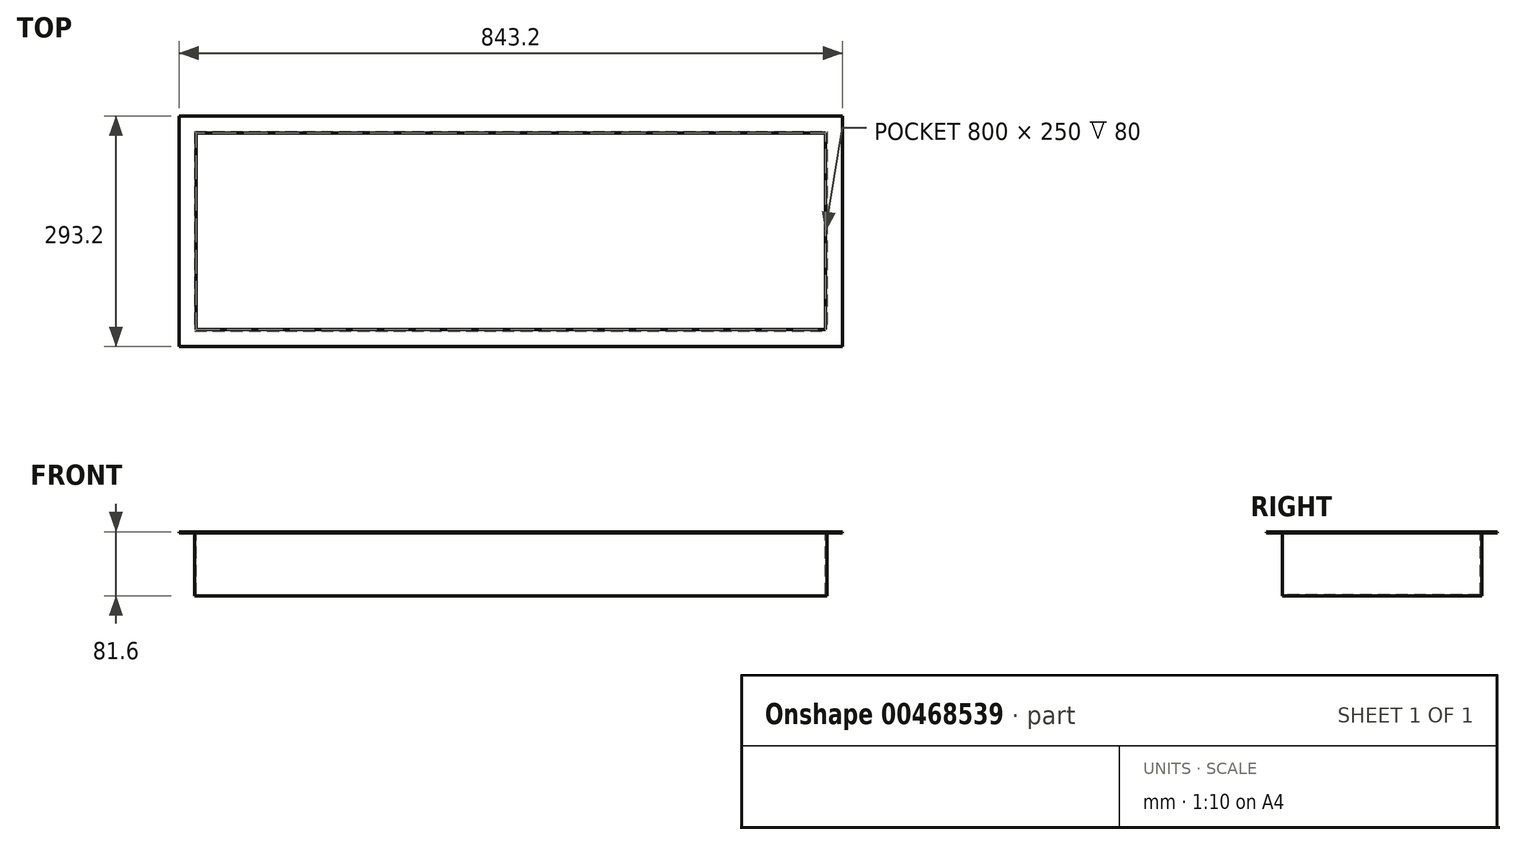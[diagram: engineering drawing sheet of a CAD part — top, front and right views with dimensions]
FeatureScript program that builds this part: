
annotation { "Feature Type Name" : "Feature", "Feature Type Description" : "" }
export const myFeature = defineFeature(function(context is Context, id is Id, definition is map)
    precondition{}
    {
        {
            var Q0;
            Q0=qCreatedBy(makeId("Top.planeOp"),FACE);
            var sketch = newSketch(context, id + "F0", { "sketchPlane" : qUnion([Q0])});
            skLineSegment(sketch, "E0.bottom", {"start": v(-398.97, -30.52) * mm, "end": v(404.23, -30.52) * mm});
            skLineSegment(sketch, "E0.top", {"start": v(-398.97, -283.72) * mm, "end": v(404.23, -283.72) * mm});
            skLineSegment(sketch, "E0.left", {"start": v(-398.97, -30.52) * mm, "end": v(-398.97, -283.72) * mm});
            skLineSegment(sketch, "E0.right", {"start": v(404.23, -30.52) * mm, "end": v(404.23, -283.72) * mm});
            skSolve(sketch);
        }
        {
            var Q0;
            Q0 = qSketchRegion(id + "F0", true);
            extrude(context, id + "F1", {"entities" : qUnion([Q0]), "depth" : 80 * mm, "offsetDistance" : 25 * mm});
        }
        {
            var Q0;
            Q0=makeQuery(id+"F1.opExtrude","CAP_FACE",FACE,{"disambiguationData":[OSD([sQuery(id+"F0.wireOp",EDGE,"E0.bottom"),sQuery(id+"F0.wireOp",EDGE,"E0.top"),sQuery(id+"F0.wireOp",EDGE,"E0.left"),sQuery(id+"F0.wireOp",EDGE,"E0.right")])],"isStart":false});
            var sketch = newSketch(context, id + "F2", { "sketchPlane" : qUnion([Q0])});
            skPoint(sketch, "E1", {"position": v(-398.97, -157.12) * mm});
            skPoint(sketch, "E2", {"position": v(404.23, -157.12) * mm});
            skPoint(sketch, "E3", {"position": v(0, -283.72) * mm});
            skPoint(sketch, "E4", {"position": v(2.63, -30.52) * mm});
            skLineSegment(sketch, "E5", {"start": v(2.63, -30.52) * mm, "end": v(0, -283.72) * mm, "construction": true});
            skLineSegment(sketch, "E6", {"start": v(-398.97, -157.12) * mm, "end": v(404.23, -157.12) * mm, "construction": true});
            skLineSegment(sketch, "E7.bottom", {"start": v(-418.97, -10.52) * mm, "end": v(424.23, -10.52) * mm});
            skLineSegment(sketch, "E7.top", {"start": v(-418.97, -303.72) * mm, "end": v(424.23, -303.72) * mm});
            skLineSegment(sketch, "E7.left", {"start": v(-418.97, -10.52) * mm, "end": v(-418.97, -303.72) * mm});
            skLineSegment(sketch, "E7.right", {"start": v(424.23, -10.52) * mm, "end": v(424.23, -303.72) * mm});
            skPoint(sketch, "E8", {"position": v(2.63, -10.52) * mm});
            skSolve(sketch);
        }
        {
            var Q0;
            Q0 = qSketchRegion(id + "F2", true);
            extrude(context, id + "F3", {"entities" : qUnion([Q0]), "operationType" : NewBodyOperationType.ADD, "depth" : 1.6 * mm, "offsetDistance" : 25 * mm});
        }
        {
            var Q0;
            Q0=makeQuery(id+"F3.opExtrude","CAP_FACE",FACE,{"disambiguationData":[OSD([sQuery(id+"F2.wireOp",EDGE,"E7.bottom"),sQuery(id+"F2.wireOp",EDGE,"E7.top"),sQuery(id+"F2.wireOp",EDGE,"E7.left"),sQuery(id+"F2.wireOp",EDGE,"E7.right")])],"isStart":false});
            var sketch = newSketch(context, id + "F4", { "sketchPlane" : qUnion([Q0])});
            skLineSegment(sketch, "E9.bottom", {"start": v(-397.37, -32.12) * mm, "end": v(402.63, -32.12) * mm});
            skLineSegment(sketch, "E9.top", {"start": v(-397.37, -282.12) * mm, "end": v(402.63, -282.12) * mm});
            skLineSegment(sketch, "E9.left", {"start": v(-397.37, -32.12) * mm, "end": v(-397.37, -282.12) * mm});
            skLineSegment(sketch, "E9.right", {"start": v(402.63, -32.12) * mm, "end": v(402.63, -282.12) * mm});
            skSolve(sketch);
        }
        {
            var Q0;
            Q0=makeQuery(id+"F4.imprint","IMPRINT",FACE,{"disambiguationData":[TD([[makeQuery(id+"F4.imprint","IMPRINT",EDGE,{"derivedFrom":sQuery(id+"F4.wireOp",EDGE,"E9.bottom")}),-1.0]])]});
            extrude(context, id + "F5", {"entities" : qUnion([Q0]), "operationType" : NewBodyOperationType.REMOVE, "oppositeDirection" : true, "depth" : 80 * mm, "offsetDistance" : 25 * mm});
        }
    });
